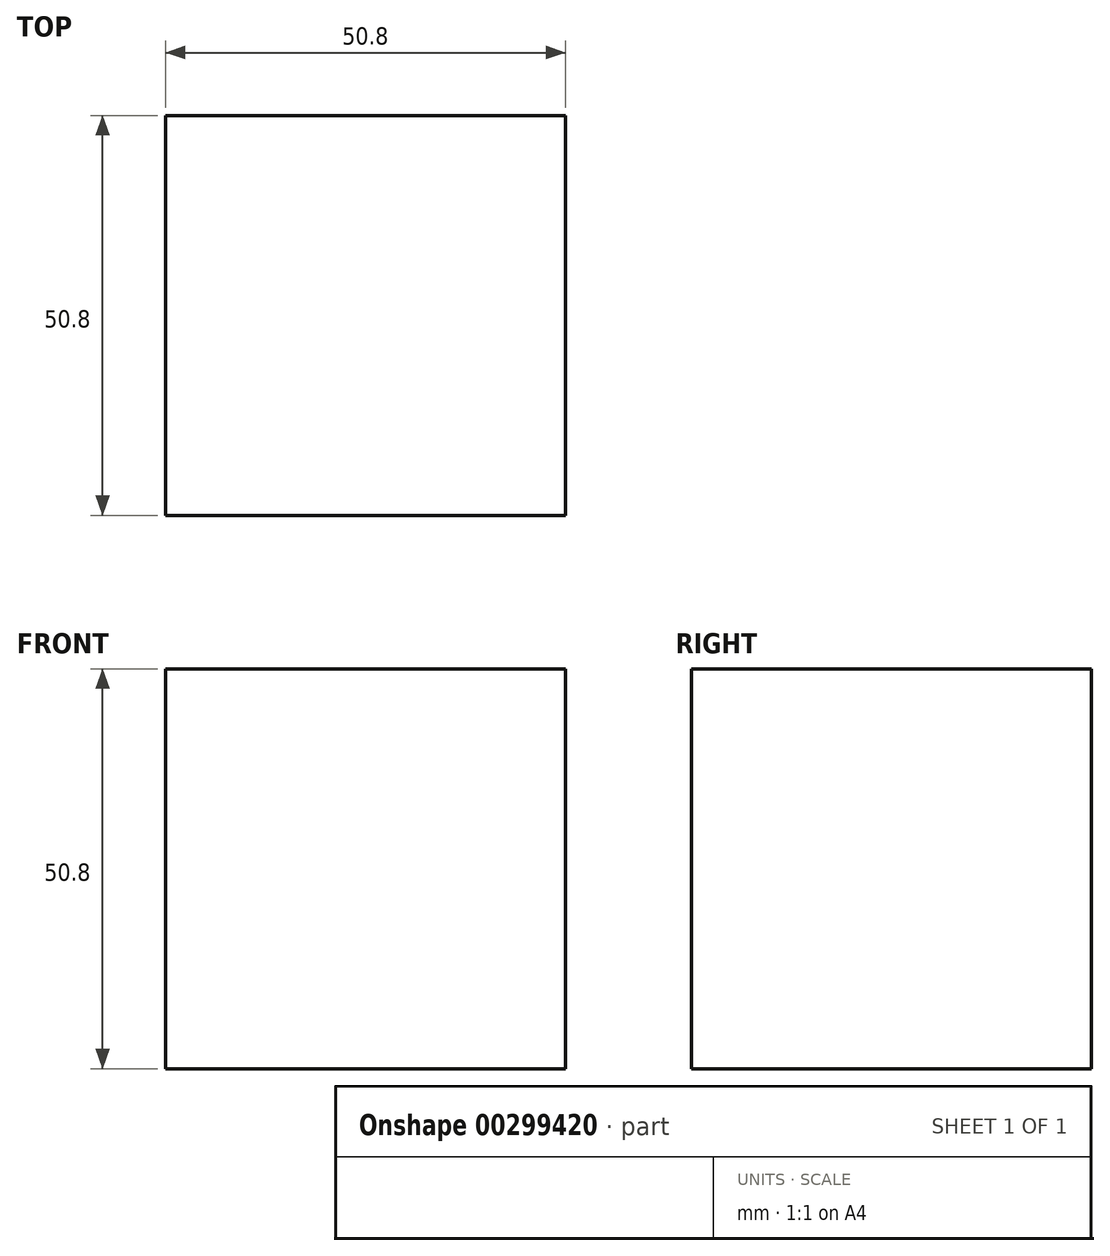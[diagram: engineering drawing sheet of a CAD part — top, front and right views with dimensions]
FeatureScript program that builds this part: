
annotation { "Feature Type Name" : "Feature", "Feature Type Description" : "" }
export const myFeature = defineFeature(function(context is Context, id is Id, definition is map)
    precondition{}
    {
        {
            var Q0;
            Q0=qCreatedBy(makeId("Front.planeOp"),FACE);
            var sketch = newSketch(context, id + "F0", { "sketchPlane" : qUnion([Q0])});
            skLineSegment(sketch, "E0.bottom", {"start": v(-50.8, 50.8) * mm, "end": v(0, 50.8) * mm});
            skLineSegment(sketch, "E0.top", {"start": v(-50.8, 0) * mm, "end": v(0, 0) * mm});
            skLineSegment(sketch, "E0.left", {"start": v(-50.8, 50.8) * mm, "end": v(-50.8, 0) * mm});
            skLineSegment(sketch, "E0.right", {"start": v(0, 50.8) * mm, "end": v(0, 0) * mm});
            skSolve(sketch);
        }
        {
            var Q0;
            Q0=makeQuery(id+"F0.imprint","IMPRINT",FACE,{"disambiguationData":[TD([[makeQuery(id+"F0.imprint","IMPRINT",EDGE,{"derivedFrom":sQuery(id+"F0.wireOp",EDGE,"E0.bottom")}),-1.0]])]});
            extrude(context, id + "F1", {"entities" : qUnion([Q0]), "depth" : 50.8 * mm});
        }
    });
